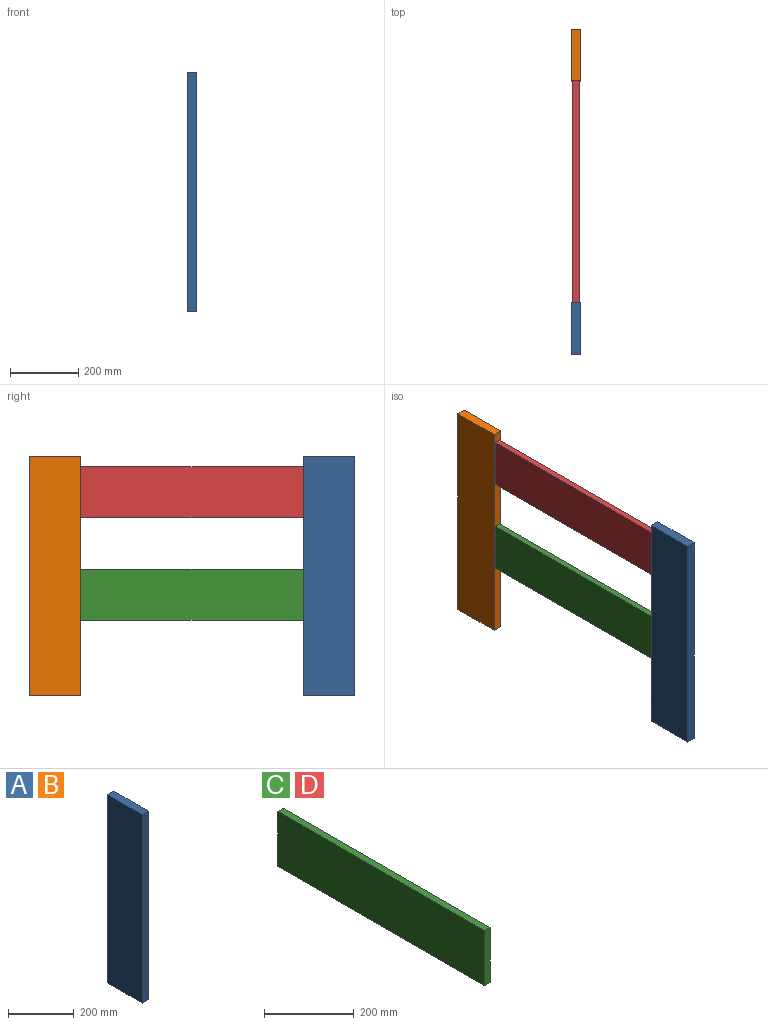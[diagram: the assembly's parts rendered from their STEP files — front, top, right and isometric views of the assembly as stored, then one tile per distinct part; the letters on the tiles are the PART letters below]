
ASSEMBLY  parts=4 mates=1
PART A: 6 faces, bbox 27x150x700 mm
  f0: plane 700x150mm, normal (1,0,0), area 105000mm2, adj f1,f3,f4,f5
  f1: plane 700x27mm, normal (0,1,0), area 18900mm2, adj f0,f2,f4,f5
  f2: plane 700x150mm, normal (-1,0,0), area 105000mm2, adj f1,f3,f4,f5
  f3: plane 700x27mm, normal (0,-1,0), area 18900mm2, adj f0,f2,f4,f5
  f4: plane 150x27mm, normal (0,0,1), area 4050mm2, adj f0,f1,f2,f3
  f5: plane 150x27mm, normal (0,0,-1), area 4050mm2, adj f0,f1,f2,f3
PART B: same geometry as A
PART C: 6 faces, bbox 18x650x150 mm
  f0: plane 650x150mm, normal (1,0,0), area 97500mm2, adj f1,f3,f4,f5
  f1: plane 650x18mm, normal (0,0,-1), area 11700mm2, adj f0,f2,f4,f5
  f2: plane 650x150mm, normal (-1,0,0), area 97500mm2, adj f1,f3,f4,f5
  f3: plane 650x18mm, normal (0,0,1), area 11700mm2, adj f0,f2,f4,f5
  f4: plane 150x18mm, normal (0,1,0), area 2700mm2, adj f0,f1,f2,f3
  f5: plane 150x18mm, normal (0,-1,0), area 2700mm2, adj f0,f1,f2,f3
PART D: same geometry as C
PLACE A at identity
PLACE B t=(0,800,0)mm
PLACE C t=(0,0,-300)mm
PLACE D at identity
MATE fastened A.f1 <-> D.f5  axis (0,1,0) through (0,75,700)mm
